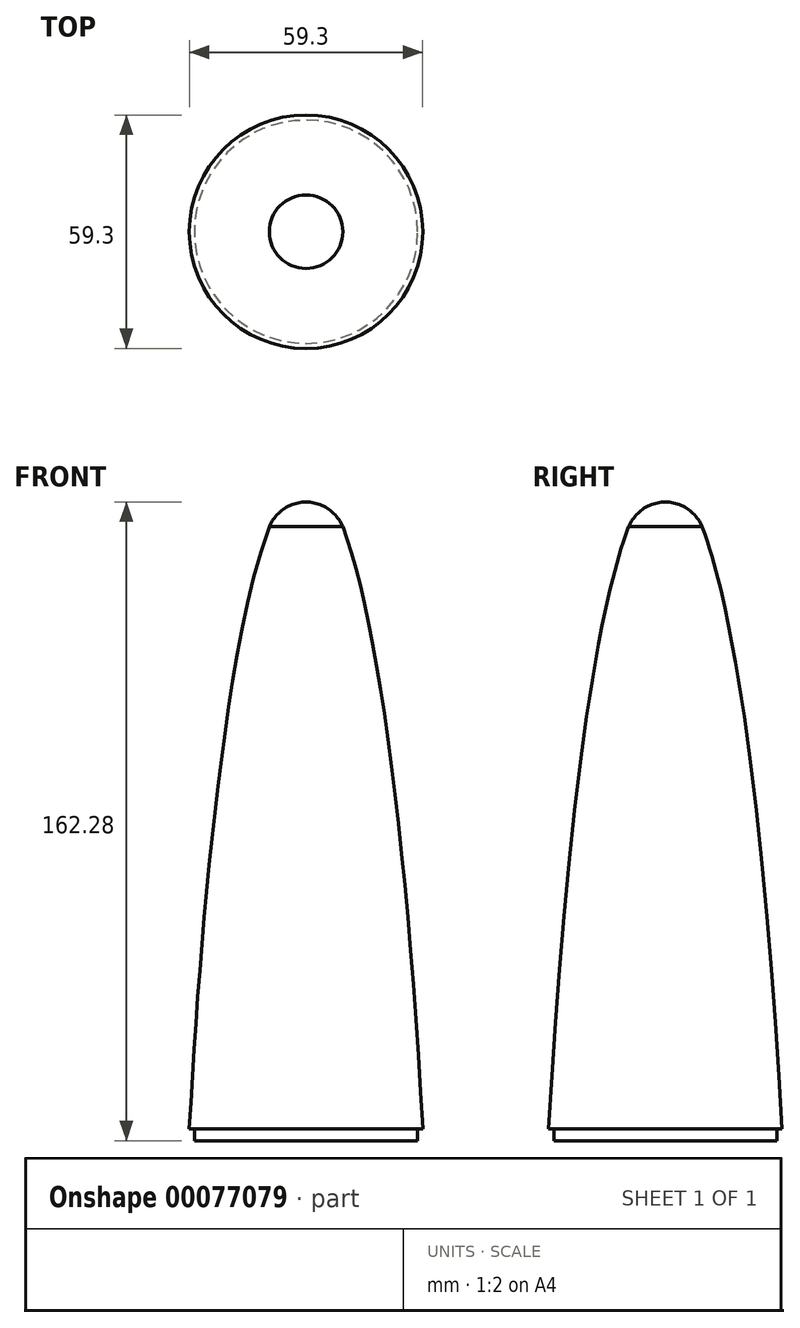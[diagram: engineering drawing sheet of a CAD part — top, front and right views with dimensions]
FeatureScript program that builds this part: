
annotation { "Feature Type Name" : "Feature", "Feature Type Description" : "" }
export const myFeature = defineFeature(function(context is Context, id is Id, definition is map)
    precondition{}
    {
        {
            var Q0;
            Q0=qCreatedBy(makeId("Front.planeOp"),FACE);
            var sketch = newSketch(context, id + "F0", { "sketchPlane" : qUnion([Q0])});
            skLineSegment(sketch, "E0", {"start": v(0, 294) * mm, "end": v(0, 129) * mm, "construction": true});
            skPoint(sketch, "E0.endSnap0", {"position": v(0, 294) * mm});
            skLineSegment(sketch, "E1.top", {"start": v(-28.36, 129) * mm, "end": v(-29.65, 129) * mm});
            skLineSegment(sketch, "E1.left", {"start": v(0, 288.28) * mm, "end": v(0, 129) * mm});
            skPoint(sketch, "E1.right.start.orphan", {"position": v(-63.28, 294) * mm});
            skPoint(sketch, "E2.orphan", {"position": v(-63.28, 129) * mm});
            skLineSegment(sketch, "E3.trimOffspring", {"start": v(0, 294) * mm, "end": v(0, -294) * mm, "construction": true});
            skLineSegment(sketch, "E4.trimOffspring", {"start": v(0, 129) * mm, "end": v(0, 288.28) * mm});
            skPoint(sketch, "E5.orphan", {"position": v(0, 67.2) * mm});
            skLineSegment(sketch, "E6.top", {"start": v(0, 126) * mm, "end": v(-28.36, 126) * mm});
            skLineSegment(sketch, "E6.left", {"start": v(0, 129) * mm, "end": v(0, 126) * mm});
            skLineSegment(sketch, "E6.right", {"start": v(-28.36, 129) * mm, "end": v(-28.36, 126) * mm});
            skPoint(sketch, "E7.center.orphan", {"position": v(0, 0) * mm});
            skEllipticalArc(sketch, "E8", {});
            skEllipticalArc(sketch, "E9", {});
            skArc(sketch, "E10", {"start": v(0, 288.28) * mm, "mid": v(-5.93, 286.3) * mm, "end": v(-9.61, 281.26) * mm});
            const initialGuessF0  = {"E8": [0, 0, 0, 1, 0.294, 0.033, 0.28678895636469665, 0.2955048098175054], "E9": [0, 0, 0, 1, 0.294, 0.033, 0.2955048098175054, 1.1165607763701657]};
            skSetInitialGuess(sketch, initialGuessF0);
            skSolve(sketch);
        }
        {
            var Q0;
            Q0=makeQuery(id+"F0.imprint","IMPRINT",FACE,{"disambiguationData":[TD([[makeQuery(id+"F0.imprint","IMPRINT",EDGE,{"derivedFrom":sQuery(id+"F0.wireOp",EDGE,"E1.top")}),-1.0]])]});
            var Q1;
            Q1=sQuery(id+"F0.wireOp",EDGE,"E3.trimOffspring");
            revolve(context, id + "F1", {"entities" : qUnion([Q0]), "axis" : qUnion([Q1]), "revolveType" : RevolveType.FULL});
        }
        {
            var Q0;
            Q0=makeQuery(id+"F1.opRevolve","SWEPT_BODY",BODY,{"disambiguationData":[OSD([sQuery(id+"F0.wireOp",EDGE,"E1.top"),sQuery(id+"F0.wireOp",EDGE,"E4.trimOffspring"),sQuery(id+"F0.wireOp",EDGE,"E6.top"),sQuery(id+"F0.wireOp",EDGE,"E6.left"),sQuery(id+"F0.wireOp",EDGE,"E6.right"),sQuery(id+"F0.wireOp",EDGE,"988e126a-8830-41c9-8f9b-90423b33b9f4"),sQuery(id+"F0.wireOp",EDGE,"6f054b1e-dafb-45bf-af7e-3cf8252b6038")])]});
            transform(context, id + "F2", {"entities" : qUnion([Q0]), "transformType" : TransformType.TRANSLATION_3D, "dx" : 0 * mm, "dy" : 0 * mm, "dz" : -220 * mm, "makeCopy" : false});
        }
    });
